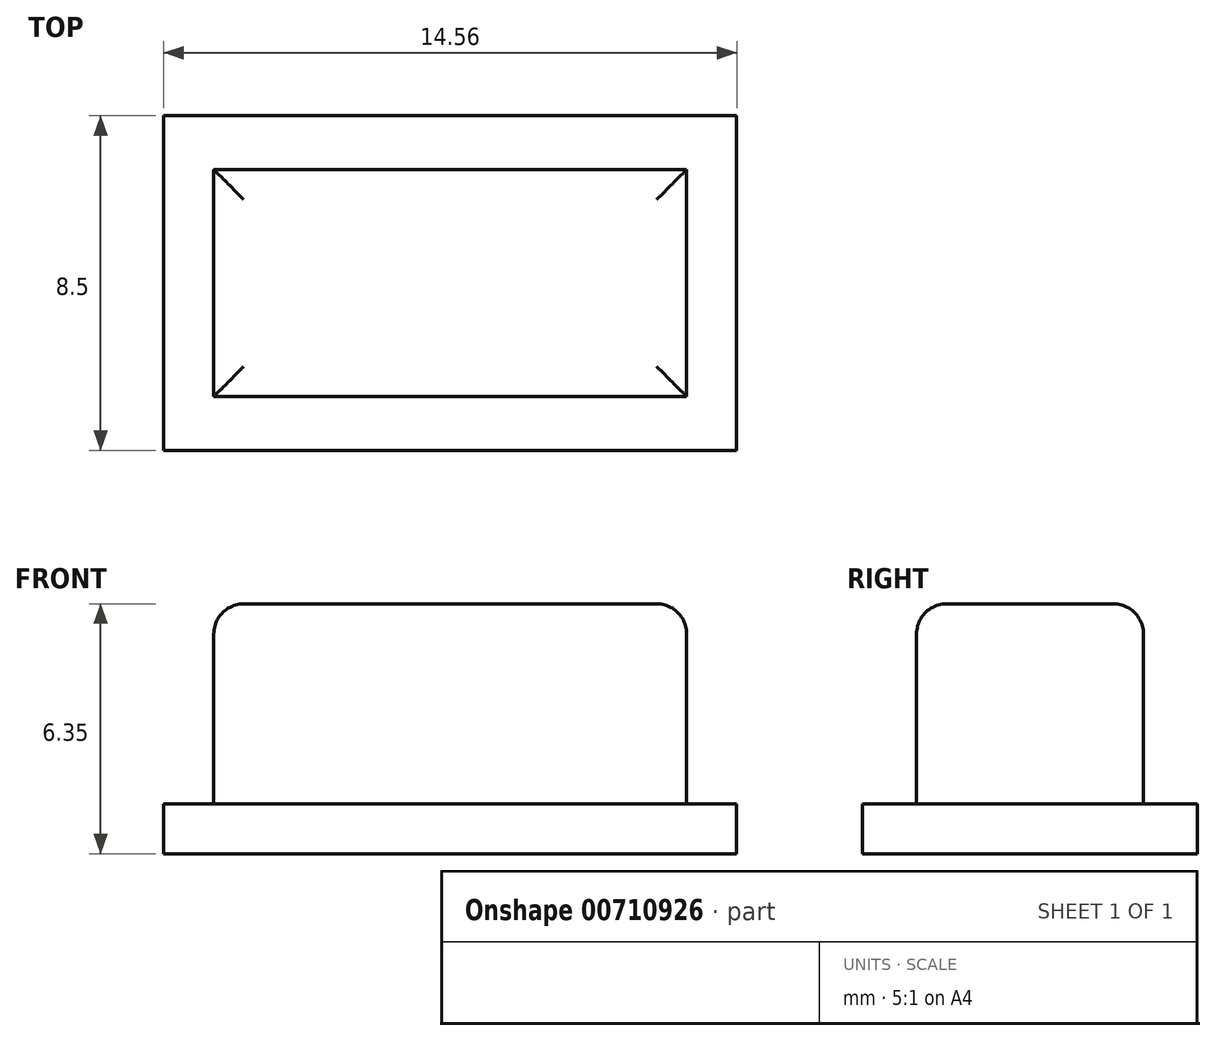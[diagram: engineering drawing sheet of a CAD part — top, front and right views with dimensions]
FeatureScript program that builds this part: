
annotation { "Feature Type Name" : "Feature", "Feature Type Description" : "" }
export const myFeature = defineFeature(function(context is Context, id is Id, definition is map)
    precondition{}
    {
        {
            var Q0;
            Q0=qCreatedBy(makeId("Top.planeOp"),FACE);
            var sketch = newSketch(context, id + "F0", { "sketchPlane" : qUnion([Q0])});
            skLineSegment(sketch, "E0.bottom", {"start": v(6, 2.88) * mm, "end": v(-6, 2.88) * mm});
            skLineSegment(sketch, "E0.top", {"start": v(6, -2.88) * mm, "end": v(-6, -2.88) * mm});
            skLineSegment(sketch, "E0.left", {"start": v(6, 2.88) * mm, "end": v(6, -2.88) * mm});
            skLineSegment(sketch, "E0.right", {"start": v(-6, 2.88) * mm, "end": v(-6, -2.88) * mm});
            skPoint(sketch, "E0.middle", {"position": v(0, 0) * mm});
            skSolve(sketch);
        }
        {
            var Q0;
            Q0=makeQuery(id+"F0.imprint","IMPRINT",FACE,{"disambiguationData":[TD([[makeQuery(id+"F0.imprint","IMPRINT",EDGE,{"derivedFrom":sQuery(id+"F0.wireOp",EDGE,"E0.bottom")}),1.0]])]});
            extrude(context, id + "F1", {"entities" : qUnion([Q0]), "depth" : 5.08 * mm, "offsetDistance" : 25.4 * mm});
        }
        {
            var Q0;
            Q0=qCreatedBy(makeId("Top.planeOp"),FACE);
            var sketch = newSketch(context, id + "F2", { "sketchPlane" : qUnion([Q0])});
            skLineSegment(sketch, "E1.bottom", {"start": v(7.28, -4.25) * mm, "end": v(-7.28, -4.25) * mm});
            skLineSegment(sketch, "E1.top", {"start": v(7.28, 4.25) * mm, "end": v(-7.28, 4.25) * mm});
            skLineSegment(sketch, "E1.left", {"start": v(7.28, -4.25) * mm, "end": v(7.28, 4.25) * mm});
            skLineSegment(sketch, "E1.right", {"start": v(-7.28, -4.25) * mm, "end": v(-7.28, 4.25) * mm});
            skPoint(sketch, "E1.middle", {"position": v(0, 0) * mm});
            skSolve(sketch);
        }
        {
            var Q0;
            Q0=makeQuery(id+"F2.imprint","IMPRINT",FACE,{"disambiguationData":[TD([[makeQuery(id+"F2.imprint","IMPRINT",EDGE,{"derivedFrom":sQuery(id+"F2.wireOp",EDGE,"E1.bottom")}),-1.0]])]});
            extrude(context, id + "F3", {"entities" : qUnion([Q0]), "operationType" : NewBodyOperationType.ADD, "oppositeDirection" : true, "depth" : 1.27 * mm, "offsetDistance" : 25.4 * mm});
        }
        {
            var Q0;
            Q0=makeQuery(id+"F1.opExtrude","CAP_FACE",FACE,{"disambiguationData":[OSD([sQuery(id+"F0.wireOp",EDGE,"E0.bottom"),sQuery(id+"F0.wireOp",EDGE,"E0.top"),sQuery(id+"F0.wireOp",EDGE,"E0.left"),sQuery(id+"F0.wireOp",EDGE,"E0.right")])],"isStart":false});
            fillet(context, id + "F4", {"entities" : qUnion([Q0]), "radius" : 0.76 * mm, "tangentPropagation" : true, "allowEdgeOverflow" : false});
        }
    });
